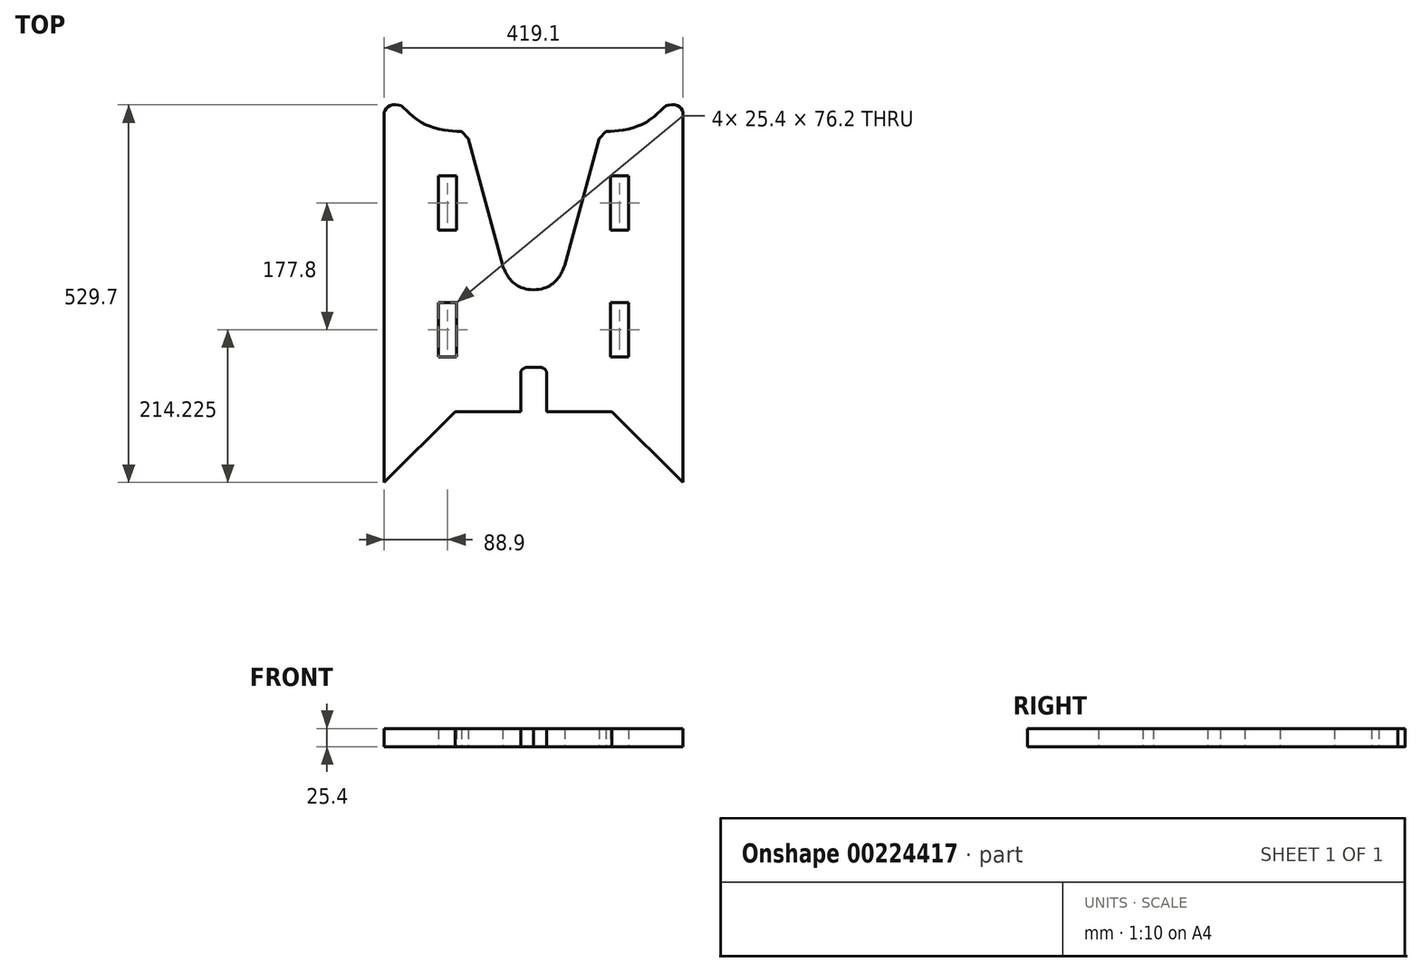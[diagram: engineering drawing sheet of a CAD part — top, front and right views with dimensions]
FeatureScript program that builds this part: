
annotation { "Feature Type Name" : "Feature", "Feature Type Description" : "" }
export const myFeature = defineFeature(function(context is Context, id is Id, definition is map)
    precondition{}
    {
        {
            var Q0;
            Q0=qCreatedBy(makeId("Top.planeOp"),FACE);
            var sketch = newSketch(context, id + "F0", { "sketchPlane" : qUnion([Q0])});
            skLineSegment(sketch, "E0", {"start": v(419.1, 29.16) * mm, "end": v(419.1, 0) * mm});
            skLineSegment(sketch, "E1", {"start": v(419.1, 0) * mm, "end": v(319.4, 99.46) * mm});
            skLineSegment(sketch, "E2", {"start": v(319.4, 99.46) * mm, "end": v(238.1, 99.46) * mm});
            skLineSegment(sketch, "E3.MirrorCS", {"start": v(99.7, 99.46) * mm, "end": v(181, 99.46) * mm});
            skLineSegment(sketch, "E4.MirrorCS", {"start": v(0, 0) * mm, "end": v(99.7, 99.46) * mm});
            skLineSegment(sketch, "E5.MirrorCS", {"start": v(0, 29.16) * mm, "end": v(0, 0) * mm});
            skLineSegment(sketch, "E6", {"start": v(0, 29.16) * mm, "end": v(0, 519.02) * mm});
            skFitSpline(sketch, "E7", {"points": [v(0, 519.02) * mm, v(0.98, 521.8) * mm, v(2.96, 524.82) * mm, v(5.2, 527.2) * mm, v(8.75, 529.17) * mm, v(14.68, 529.7) * mm, v(20.73, 529.43) * mm, v(24.82, 527.72) * mm, v(31.66, 521.4) * mm, v(40.62, 512.97) * mm, v(54.58, 503.75) * mm, v(67.22, 498.49) * mm, v(83.8, 494.27) * mm, v(95.8, 492.82) * mm, v(108.17, 492.3) * mm], "startDerivative": vector(17, 69.44) * mm, "endDerivative": vector(143.4, -4.56) * mm});
            skLineSegment(sketch, "E8", {"start": v(108.17, 492.3) * mm, "end": v(117.8, 482.43) * mm});
            skLineSegment(sketch, "E9", {"start": v(117.8, 482.43) * mm, "end": v(165.93, 304.68) * mm});
            skFitSpline(sketch, "E10", {"points": [v(165.93, 304.68) * mm, v(209.55, 270.35) * mm], "startDerivative": vector(10.72, -29.36) * mm, "endDerivative": vector(91.67, 0) * mm});
            skLineSegment(sketch, "E11", {"start": v(191.26, 99.46) * mm, "end": v(191.26, 153.84) * mm});
            skFitSpline(sketch, "E12", {"points": [v(191.26, 153.84) * mm, v(191.99, 156.35) * mm, v(193.69, 158.58) * mm, v(195.9, 160.34) * mm, v(199.44, 161.51) * mm, v(209.55, 161.78) * mm], "startDerivative": vector(0, 14.5) * mm, "endDerivative": vector(35.86, -0.42) * mm});
            skPoint(sketch, "E13.trimOffspring.end.orphan", {"position": v(419.1, 29.16) * mm});
            skLineSegment(sketch, "E14.MirrorCS", {"start": v(310.93, 492.3) * mm, "end": v(301.3, 482.43) * mm});
            skFitSpline(sketch, "E15.MirrorCS", {"points": [v(227.84, 153.84) * mm, v(227.11, 156.35) * mm, v(225.41, 158.58) * mm, v(223.2, 160.34) * mm, v(219.66, 161.51) * mm, v(209.55, 161.78) * mm], "startDerivative": vector(0, 14.5) * mm, "endDerivative": vector(-35.86, -0.42) * mm});
            skFitSpline(sketch, "E16.MirrorCS", {"points": [v(419.1, 519.02) * mm, v(418.12, 521.8) * mm, v(416.14, 524.82) * mm, v(413.9, 527.2) * mm, v(410.35, 529.17) * mm, v(404.42, 529.7) * mm, v(398.37, 529.43) * mm, v(394.28, 527.72) * mm, v(387.44, 521.4) * mm, v(378.48, 512.97) * mm, v(364.52, 503.75) * mm, v(351.88, 498.49) * mm, v(335.3, 494.27) * mm, v(323.3, 492.82) * mm, v(310.93, 492.3) * mm], "startDerivative": vector(-17, 69.44) * mm, "endDerivative": vector(-143.4, -4.56) * mm});
            skFitSpline(sketch, "E17.MirrorCS", {"points": [v(253.17, 304.68) * mm, v(209.55, 270.35) * mm], "startDerivative": vector(-10.72, -29.36) * mm, "endDerivative": vector(-91.67, 0) * mm});
            skLineSegment(sketch, "E18.MirrorCS", {"start": v(301.3, 482.43) * mm, "end": v(253.17, 304.68) * mm});
            skLineSegment(sketch, "E19.MirrorCS", {"start": v(419.1, 29.16) * mm, "end": v(419.1, 519.02) * mm});
            skLineSegment(sketch, "E20.MirrorCS", {"start": v(227.84, 99.46) * mm, "end": v(227.84, 153.84) * mm});
            skLineSegment(sketch, "E21", {"start": v(99.7, 99.46) * mm, "end": v(191.26, 99.46) * mm});
            skLineSegment(sketch, "E22.trimOffspring", {"start": v(227.84, 99.46) * mm, "end": v(319.4, 99.46) * mm});
            skLineSegment(sketch, "E23.bottom", {"start": v(101.6, 353.92) * mm, "end": v(76.2, 353.92) * mm});
            skLineSegment(sketch, "E23.top", {"start": v(101.6, 430.12) * mm, "end": v(76.2, 430.12) * mm});
            skLineSegment(sketch, "E23.left", {"start": v(101.6, 353.92) * mm, "end": v(101.6, 430.12) * mm});
            skLineSegment(sketch, "E23.right", {"start": v(76.2, 353.92) * mm, "end": v(76.2, 430.12) * mm});
            skPoint(sketch, "E23.middle", {"position": v(88.9, 392.02) * mm});
            skLineSegment(sketch, "E24.bottom", {"start": v(101.6, 252.32) * mm, "end": v(76.2, 252.32) * mm});
            skLineSegment(sketch, "E24.top", {"start": v(101.6, 176.12) * mm, "end": v(76.2, 176.12) * mm});
            skLineSegment(sketch, "E24.left", {"start": v(101.6, 252.32) * mm, "end": v(101.6, 176.12) * mm});
            skLineSegment(sketch, "E24.right", {"start": v(76.2, 252.32) * mm, "end": v(76.2, 176.12) * mm});
            skPoint(sketch, "E24.middle", {"position": v(88.9, 214.22) * mm});
            skLineSegment(sketch, "E25.MirrorCS", {"start": v(317.5, 176.12) * mm, "end": v(342.9, 176.12) * mm});
            skLineSegment(sketch, "E26.MirrorCS", {"start": v(317.5, 430.12) * mm, "end": v(342.9, 430.12) * mm});
            skLineSegment(sketch, "E27.MirrorCS", {"start": v(342.9, 252.32) * mm, "end": v(342.9, 176.12) * mm});
            skLineSegment(sketch, "E28.MirrorCS", {"start": v(342.9, 353.92) * mm, "end": v(342.9, 430.12) * mm});
            skPoint(sketch, "E29.MirrorP", {"position": v(330.2, 392.02) * mm});
            skPoint(sketch, "E30.MirrorP", {"position": v(330.2, 214.22) * mm});
            skLineSegment(sketch, "E31.MirrorCS", {"start": v(317.5, 252.32) * mm, "end": v(342.9, 252.32) * mm});
            skLineSegment(sketch, "E32.MirrorCS", {"start": v(317.5, 353.92) * mm, "end": v(342.9, 353.92) * mm});
            skLineSegment(sketch, "E33.MirrorCS", {"start": v(317.5, 353.92) * mm, "end": v(317.5, 430.12) * mm});
            skLineSegment(sketch, "E34.MirrorCS", {"start": v(317.5, 252.32) * mm, "end": v(317.5, 176.12) * mm});
            skSolve(sketch);
        }
        {
            var Q0;
            Q0 = qSketchRegion(id + "F0", true);
            extrude(context, id + "F1", {"entities" : qUnion([Q0]), "depth" : 25.4 * mm});
        }
    });
